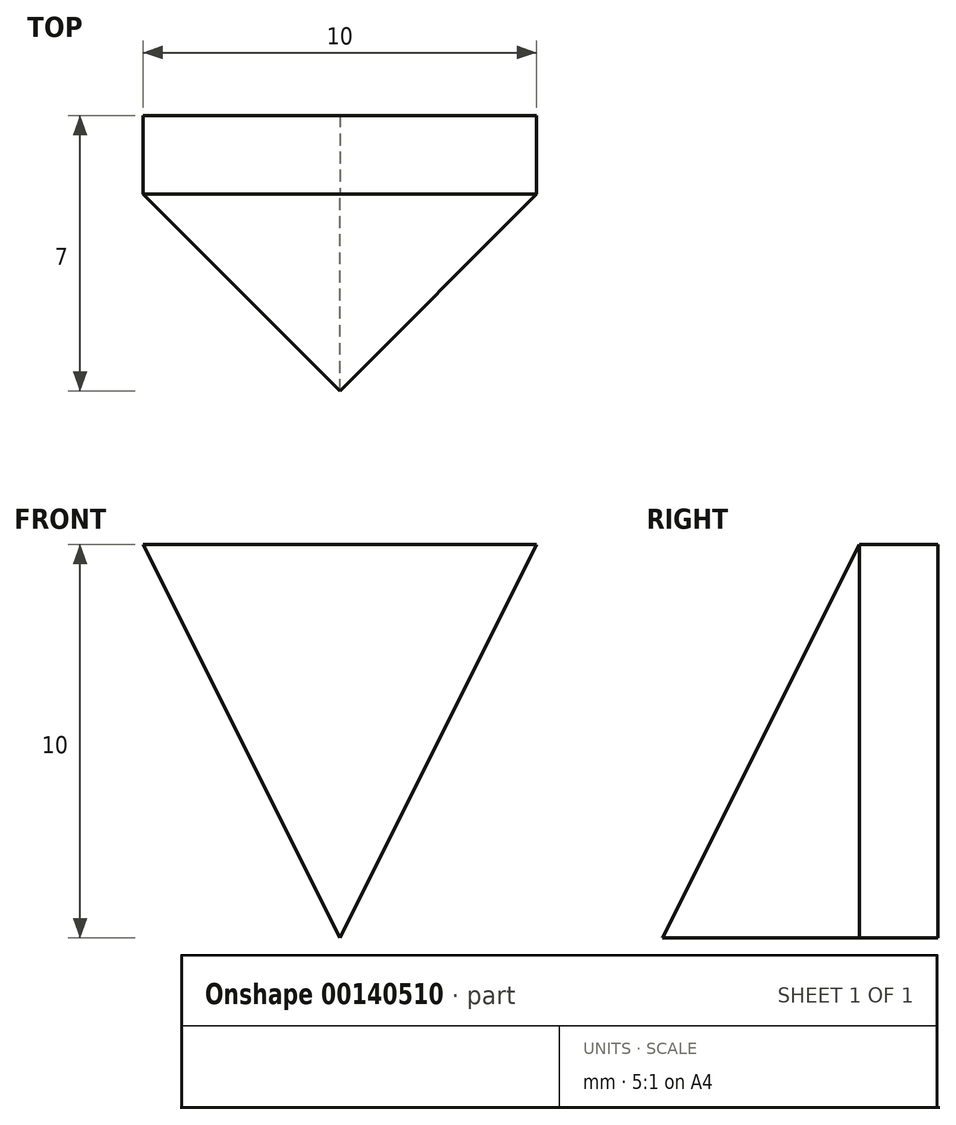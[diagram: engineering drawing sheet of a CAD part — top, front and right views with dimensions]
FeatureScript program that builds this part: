
annotation { "Feature Type Name" : "Feature", "Feature Type Description" : "" }
export const myFeature = defineFeature(function(context is Context, id is Id, definition is map)
    precondition{}
    {
        {
            var Q0;
            Q0=qCreatedBy(makeId("Front.planeOp"),FACE);
            var sketch = newSketch(context, id + "F0", { "sketchPlane" : qUnion([Q0])});
            skLineSegment(sketch, "E0", {"start": v(0, 0) * mm, "end": v(5, 0) * mm});
            skLineSegment(sketch, "E1", {"start": v(5, 0) * mm, "end": v(10, 0) * mm});
            skLineSegment(sketch, "E2", {"start": v(10, 0) * mm, "end": v(5, -10) * mm});
            skLineSegment(sketch, "E3", {"start": v(5, -10) * mm, "end": v(0, 0) * mm});
            skLineSegment(sketch, "E4.0", {"start": v(5, -1) * mm, "end": v(8.38, -1) * mm});
            skLineSegment(sketch, "E4.1", {"start": v(1.62, -1) * mm, "end": v(5, -1) * mm});
            skLineSegment(sketch, "E4.2", {"start": v(5, -7.76) * mm, "end": v(1.62, -1) * mm});
            skLineSegment(sketch, "E4.3", {"start": v(8.38, -1) * mm, "end": v(5, -7.76) * mm});
            skLineSegment(sketch, "E5", {"start": v(0, 0) * mm, "end": v(0, -12.62) * mm});
            skLineSegment(sketch, "E6", {"start": v(10, 0) * mm, "end": v(10, -11.75) * mm});
            skSolve(sketch);
        }
        {
            var Q0;
            Q0=qCreatedBy(makeId("Right.planeOp"),FACE);
            var sketch = newSketch(context, id + "F1", { "sketchPlane" : qUnion([Q0])});
            skLineSegment(sketch, "E7", {"start": v(0, 0) * mm, "end": v(0, -10) * mm});
            skLineSegment(sketch, "E8", {"start": v(0, -10) * mm, "end": v(-15, -10) * mm});
            skLineSegment(sketch, "E9", {"start": v(0, 0) * mm, "end": v(-7.88, -15.77) * mm});
            skLineSegment(sketch, "E10", {"start": v(0, 0) * mm, "end": v(-20.08, 0) * mm});
            skLineSegment(sketch, "E11", {"start": v(-20.08, 0) * mm, "end": v(-20.08, -10) * mm});
            skLineSegment(sketch, "E12", {"start": v(-20.08, -10) * mm, "end": v(-15, -10) * mm});
            skSolve(sketch);
        }
        {
            var Q0;
            Q0=makeQuery(id+"F0.imprint","IMPRINT",FACE,{"disambiguationData":[TD([[makeQuery(id+"F0.imprint","IMPRINT",EDGE,{"derivedFrom":sQuery(id+"F0.wireOp",EDGE,"E4.0")}),-1.0]])]});
            var Q1;
            Q1=makeQuery(id+"F0.imprint","IMPRINT",FACE,{"disambiguationData":[TD([[makeQuery(id+"F0.imprint","IMPRINT",EDGE,{"derivedFrom":sQuery(id+"F0.wireOp",EDGE,"E0")}),-1.0]])]});
            extrude(context, id + "F2", {"entities" : qUnion([Q0, Q1]), "oppositeDirection" : true, "depth" : 2 * mm});
        }
        {
            var Q0;
            Q0=makeQuery(id+"F0.imprint","IMPRINT",FACE,{"disambiguationData":[TD([[makeQuery(id+"F0.imprint","IMPRINT",EDGE,{"derivedFrom":sQuery(id+"F0.wireOp",EDGE,"E4.0")}),-1.0]])]});
            var Q1;
            Q1=makeQuery(id+"F0.imprint","IMPRINT",FACE,{"disambiguationData":[TD([[makeQuery(id+"F0.imprint","IMPRINT",EDGE,{"derivedFrom":sQuery(id+"F0.wireOp",EDGE,"E0")}),-1.0]])]});
            extrude(context, id + "F3", {"entities" : qUnion([Q0, Q1]), "depth" : 10 * mm});
        }
        {
            var Q0;
            {var subQ0=sQuery(id+"F1.wireOp",EDGE,"E10");Q0=makeQuery(id+"F1.imprint","IMPRINT",FACE,{"disambiguationData":[TD([[makeQuery(id+"F1.imprint","IMPRINT",EDGE,{"derivedFrom":subQ0}),1.0]])]});}
            extrude(context, id + "F4", {"entities" : qUnion([Q0]), "operationType" : NewBodyOperationType.REMOVE, "endBound" : BoundingType.THROUGH_ALL, "depth" : 25 * mm});
        }
    });
